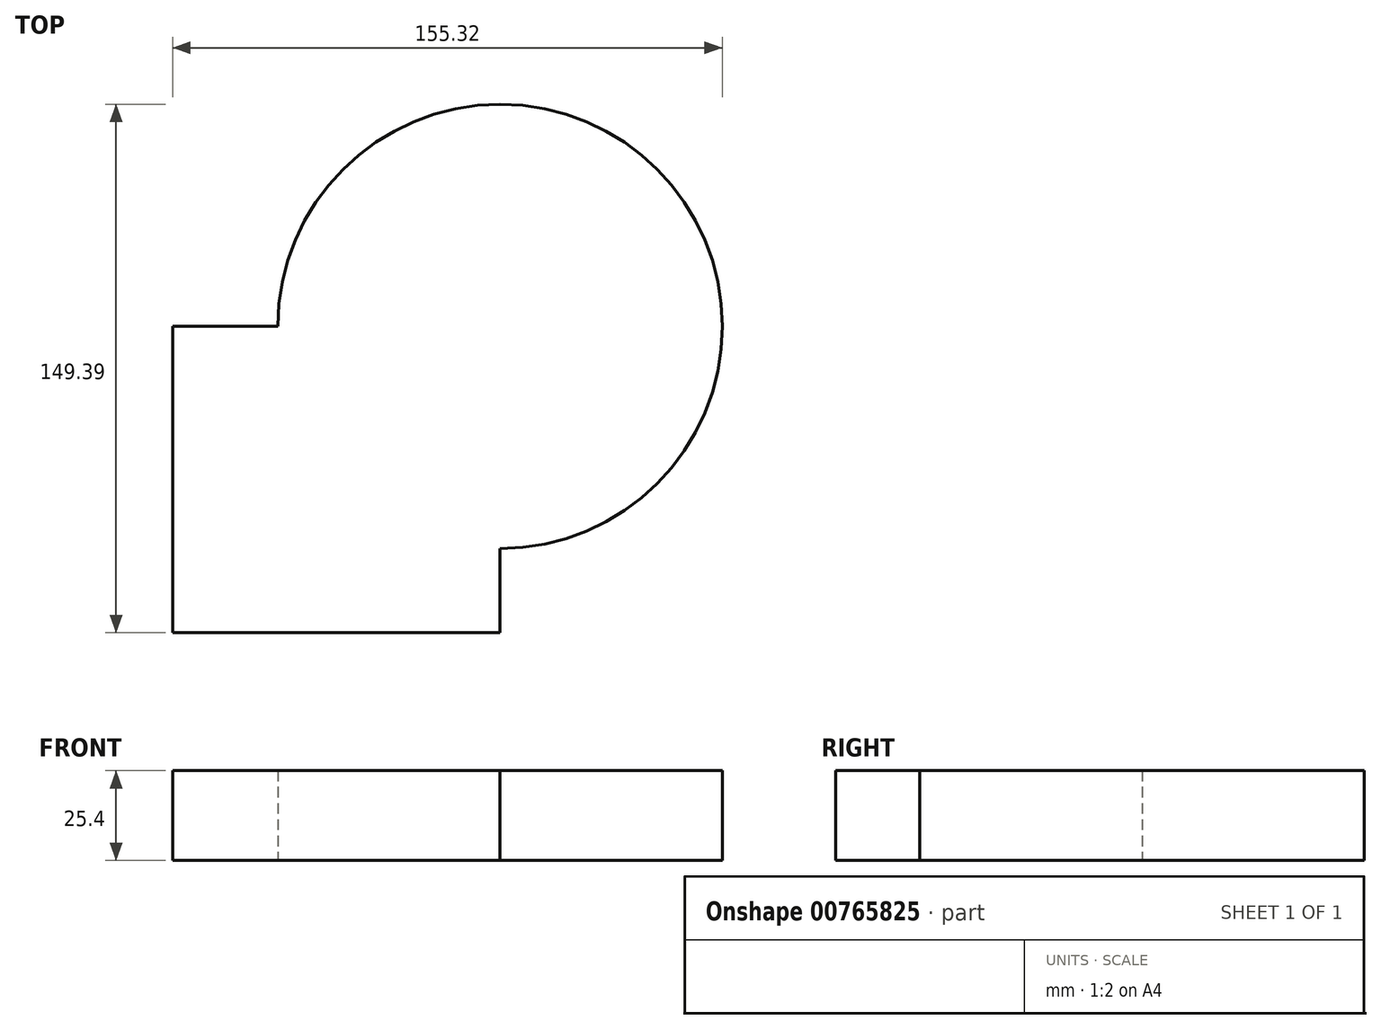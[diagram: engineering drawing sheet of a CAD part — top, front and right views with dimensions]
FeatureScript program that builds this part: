
annotation { "Feature Type Name" : "Feature", "Feature Type Description" : "" }
export const myFeature = defineFeature(function(context is Context, id is Id, definition is map)
    precondition{}
    {
        {
            var Q0;
            Q0=qCreatedBy(makeId("Top.planeOp"),FACE);
            var sketch = newSketch(context, id + "F0", { "sketchPlane" : qUnion([Q0])});
            skLineSegment(sketch, "E0.bottom", {"start": v(-130.74, -40.74) * mm, "end": v(-38.23, -40.74) * mm});
            skLineSegment(sketch, "E0.top", {"start": v(-130.74, -127.33) * mm, "end": v(-38.23, -127.33) * mm});
            skLineSegment(sketch, "E0.left", {"start": v(-130.74, -40.74) * mm, "end": v(-130.74, -127.33) * mm});
            skLineSegment(sketch, "E0.right", {"start": v(-38.23, -40.74) * mm, "end": v(-38.23, -127.33) * mm});
            skCircle(sketch, "E1", {"center": v(-38.23, -40.74) * mm, "radius": 62.8 * mm});
            skSolve(sketch);
        }
        {
            var Q0;
            {var subQ0=sQuery(id+"F0.wireOp",EDGE,"E0.right");var subQ1=sQuery(id+"F0.wireOp",EDGE,"E0.bottom");var subQ2=makeQuery(id+"F0.imprint","INTERSECT",VERTEX,{"derivedFrom":[subQ1,subQ0]});Q0=makeQuery(id+"F0.imprint","IMPRINT",FACE,{"disambiguationData":[TD([[makeQuery(id+"F0.imprint","IMPRINT",EDGE,{"disambiguationData":[TD([[subQ2,1.0]])],"derivedFrom":subQ1}),-1.0]])]});}
            var Q1;
            {var subQ1=sQuery(id+"F0.wireOp",EDGE,"E0.top");Q1=makeQuery(id+"F0.imprint","IMPRINT",FACE,{"disambiguationData":[TD([[makeQuery(id+"F0.imprint","IMPRINT",EDGE,{"derivedFrom":subQ1}),1.0]])]});}
            var Q2;
            {var subQ0=sQuery(id+"F0.wireOp",EDGE,"E0.right");var subQ1=sQuery(id+"F0.wireOp",EDGE,"E0.bottom");var subQ2=makeQuery(id+"F0.imprint","INTERSECT",VERTEX,{"derivedFrom":[subQ1,subQ0]});Q2=makeQuery(id+"F0.imprint","IMPRINT",FACE,{"disambiguationData":[TD([[makeQuery(id+"F0.imprint","IMPRINT",EDGE,{"disambiguationData":[TD([[subQ2,1.0]])],"derivedFrom":subQ1}),1.0]])]});}
            extrude(context, id + "F1", {"entities" : qUnion([Q0, Q1, Q2]), "depth" : 25.4 * mm, "offsetDistance" : 25.4 * mm});
        }
    });
